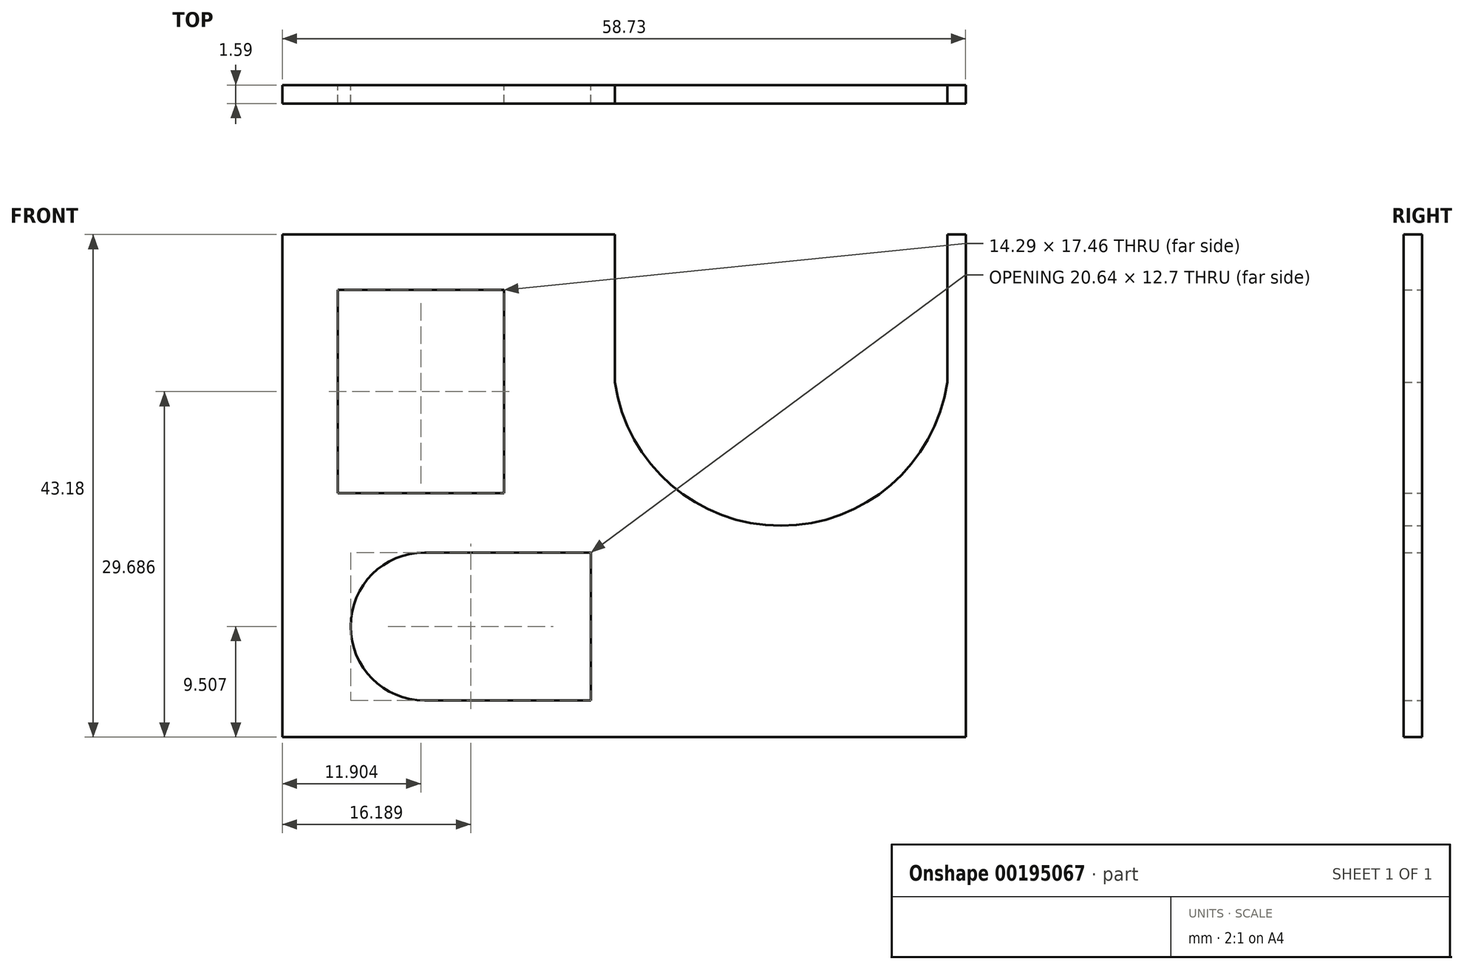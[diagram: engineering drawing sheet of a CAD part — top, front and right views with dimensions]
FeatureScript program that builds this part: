
annotation { "Feature Type Name" : "Feature", "Feature Type Description" : "" }
export const myFeature = defineFeature(function(context is Context, id is Id, definition is map)
    precondition{}
    {
        {
            var Q0;
            Q0=qCreatedBy(makeId("Front.planeOp"),FACE);
            var sketch = newSketch(context, id + "F0", { "sketchPlane" : qUnion([Q0])});
            skLineSegment(sketch, "E0.top", {"start": v(-30.16, -17.78) * mm, "end": v(28.58, -17.78) * mm});
            skLineSegment(sketch, "E0.left", {"start": v(-30.16, 25.4) * mm, "end": v(-30.16, -17.78) * mm});
            skLineSegment(sketch, "E0.right", {"start": v(28.58, 25.4) * mm, "end": v(28.58, -17.78) * mm});
            skLineSegment(sketch, "E1.bottom", {"start": v(-25.4, 20.64) * mm, "end": v(-11.11, 20.64) * mm});
            skLineSegment(sketch, "E1.top", {"start": v(-25.4, 3.17) * mm, "end": v(-11.11, 3.17) * mm});
            skLineSegment(sketch, "E1.left", {"start": v(-25.4, 20.64) * mm, "end": v(-25.4, 3.17) * mm});
            skLineSegment(sketch, "E1.right", {"start": v(-11.11, 20.64) * mm, "end": v(-11.11, 3.17) * mm});
            skLineSegment(sketch, "E2.bottom", {"start": v(-17.94, -1.92) * mm, "end": v(-3.65, -1.92) * mm});
            skLineSegment(sketch, "E2.top", {"start": v(-17.94, -14.62) * mm, "end": v(-3.65, -14.62) * mm});
            skLineSegment(sketch, "E2.right", {"start": v(-3.65, -1.92) * mm, "end": v(-3.65, -14.62) * mm});
            skArc(sketch, "E3", {"start": v(-1.59, 12.7) * mm, "mid": v(12.7, 0.37) * mm, "end": v(26.99, 12.7) * mm});
            skLineSegment(sketch, "E4", {"start": v(-1.59, 12.7) * mm, "end": v(-1.59, 25.4) * mm});
            skLineSegment(sketch, "E5", {"start": v(26.99, 12.7) * mm, "end": v(26.99, 25.4) * mm});
            skLineSegment(sketch, "E6", {"start": v(-30.16, 25.4) * mm, "end": v(-1.59, 25.4) * mm});
            skPoint(sketch, "E7", {"position": v(-24.29, -8.27) * mm});
            skArc(sketch, "E8", {"start": v(-17.94, -1.92) * mm, "mid": v(-24.29, -8.27) * mm, "end": v(-17.94, -14.62) * mm});
            skLineSegment(sketch, "E9", {"start": v(26.99, 25.4) * mm, "end": v(28.58, 25.4) * mm});
            skSolve(sketch);
        }
        {
            var Q0;
            Q0 = qSketchRegion(id + "F0", true);
            extrude(context, id + "F1", {"entities" : qUnion([Q0]), "depth" : 1.59 * mm});
        }
    });
